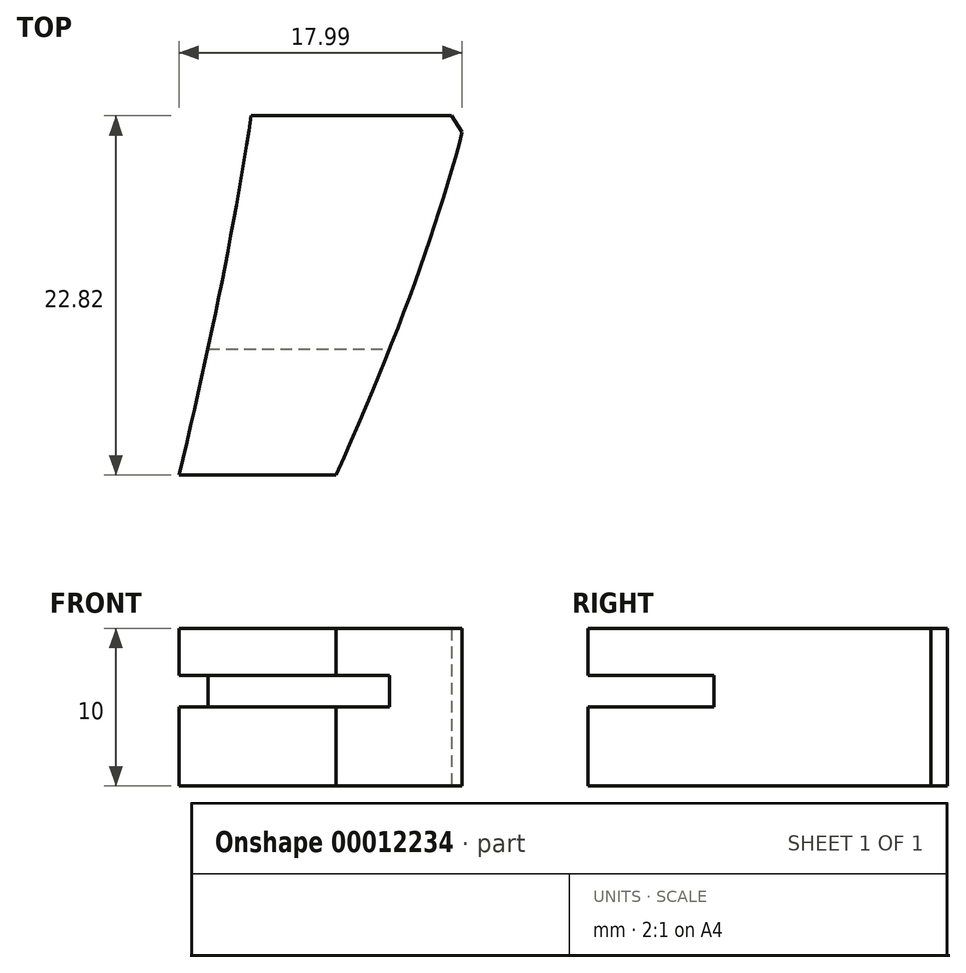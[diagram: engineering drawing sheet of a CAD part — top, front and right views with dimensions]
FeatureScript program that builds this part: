
annotation { "Feature Type Name" : "Feature", "Feature Type Description" : "" }
export const myFeature = defineFeature(function(context is Context, id is Id, definition is map)
    precondition{}
    {
        {
            var Q0;
            Q0=qCreatedBy(makeId("Top.planeOp"),FACE);
            var sketch = newSketch(context, id + "F0", { "sketchPlane" : qUnion([Q0])});
            skText(sketch, "E0", { "text": ",", "fontName": "OpenSans-Bold.ttf"});
            const initialGuessF0  = {"E0": [-0.02688, 0, 1, 0, 0.067]};
            skSetInitialGuess(sketch, initialGuessF0);
            skSolve(sketch);
        }
        {
            var Q0;
            Q0=makeQuery(id+"F0.imprint","IMPRINT",FACE,{"disambiguationData":[TD([[makeQuery(id+"F0.imprint","IMPRINT",EDGE,{"derivedFrom":sQuery(id+"F0.wireOp",EDGE,"E0.sketch_text.stroke-0")}),-1.0]])]});
            extrude(context, id + "F1", {"entities" : qUnion([Q0]), "depth" : 10 * mm});
        }
        {
            var Q0;
            Q0=makeQuery(id+"F1.opExtrude","SWEPT_FACE",FACE,{"disambiguationData":[OSD([sQuery(id+"F0.wireOp",EDGE,"E0.sketch_text.stroke-1")])]});
            var sketch = newSketch(context, id + "F2", { "sketchPlane" : qUnion([Q0])});
            skLineSegment(sketch, "E1.bottom", {"start": v(-24.02, 5) * mm, "end": v(-4.6, 5) * mm});
            skLineSegment(sketch, "E1.top", {"start": v(-24.02, 7) * mm, "end": v(-4.6, 7) * mm});
            skLineSegment(sketch, "E1.left", {"start": v(-24.02, 5) * mm, "end": v(-24.02, 7) * mm});
            skLineSegment(sketch, "E1.right", {"start": v(-4.6, 5) * mm, "end": v(-4.6, 7) * mm});
            skSolve(sketch);
        }
        {
            var Q0;
            Q0 = qSketchRegion(id + "F2", true);
            extrude(context, id + "F3", {"entities" : qUnion([Q0]), "operationType" : NewBodyOperationType.REMOVE, "oppositeDirection" : true, "depth" : 8 * mm});
        }
    });
